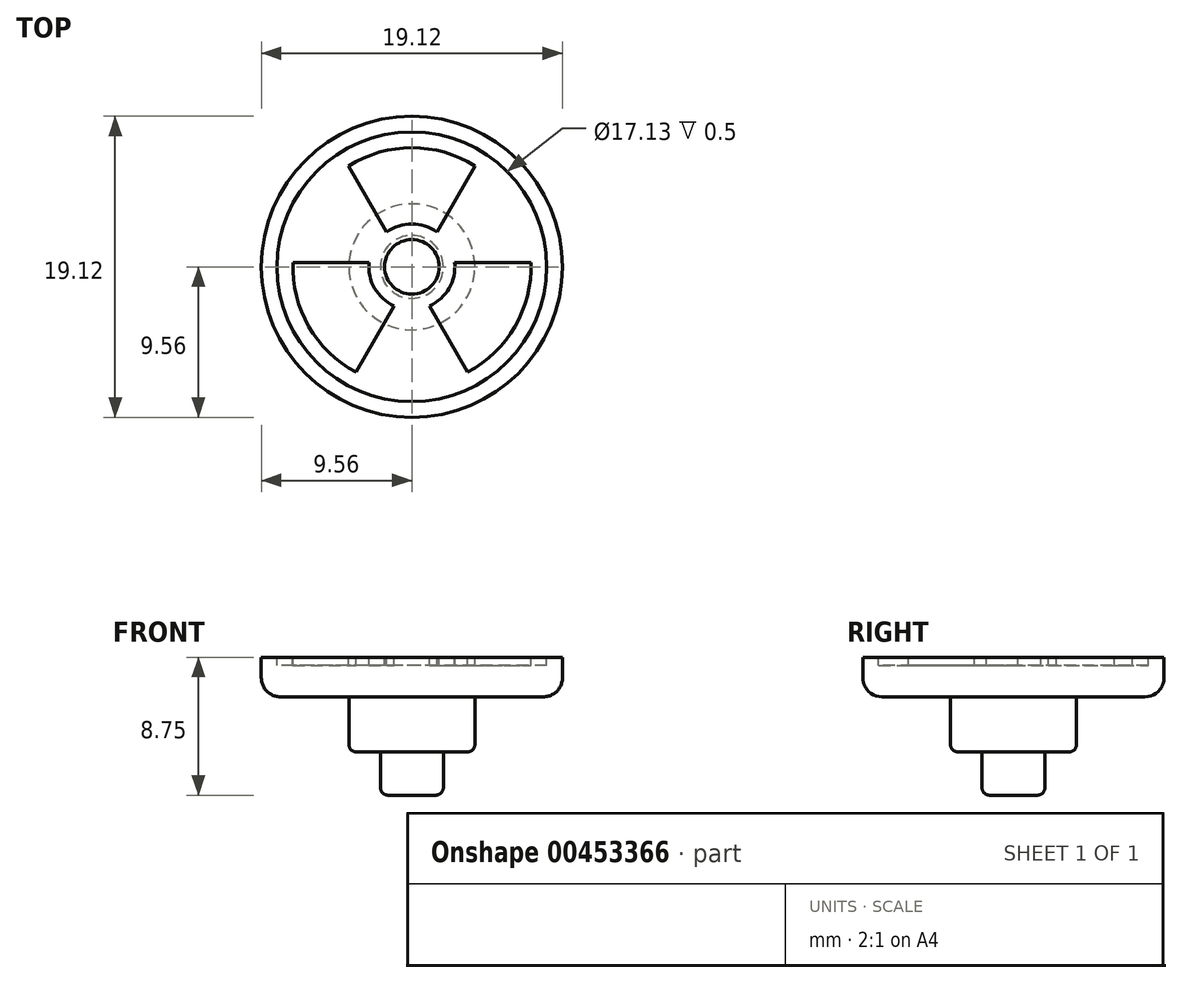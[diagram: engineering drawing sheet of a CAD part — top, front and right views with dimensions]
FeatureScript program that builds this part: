
annotation { "Feature Type Name" : "Feature", "Feature Type Description" : "" }
export const myFeature = defineFeature(function(context is Context, id is Id, definition is map)
    precondition{}
    {
        {
            var Q0;
            Q0=qCreatedBy(makeId("Top.planeOp"),FACE);
            var sketch = newSketch(context, id + "F0", { "sketchPlane" : qUnion([Q0])});
            skCircle(sketch, "E0", {"center": v(0, 0) * mm, "radius": 9.56 * mm});
            skSolve(sketch);
        }
        {
            var Q0;
            Q0=makeQuery(id+"F0.imprint","IMPRINT",FACE,{"disambiguationData":[TD([[makeQuery(id+"F0.imprint","IMPRINT",EDGE,{"derivedFrom":sQuery(id+"F0.wireOp",EDGE,"E0")}),1.0]])]});
            extrude(context, id + "F1", {"entities" : qUnion([Q0]), "depth" : 2.5 * mm, "offsetDistance" : 25 * mm});
        }
        {
            var Q0;
            Q0=makeQuery(id+"F1.opExtrude","CAP_FACE",FACE,{"disambiguationData":[OSD([sQuery(id+"F0.wireOp",EDGE,"E0")])],"isStart":false});
            var sketch = newSketch(context, id + "F2", { "sketchPlane" : qUnion([Q0])});
            skCircle(sketch, "E1", {"center": v(0, 0) * mm, "radius": 1.73 * mm});
            skArc(sketch, "E2", {"start": v(1.6, 2.22) * mm, "mid": v(0, 2.73) * mm, "end": v(-1.6, 2.22) * mm});
            skLineSegment(sketch, "E3", {"start": v(-1.6, 2.22) * mm, "end": v(-4.52, 7.28) * mm});
            skLineSegment(sketch, "E4", {"start": v(1.6, 2.22) * mm, "end": v(4.52, 7.28) * mm});
            skArc(sketch, "E5", {"start": v(4.52, 7.28) * mm, "mid": v(0, 8.56) * mm, "end": v(-4.52, 7.28) * mm});
            skLineSegment(sketch, "E6", {"start": v(0, 0) * mm, "end": v(8.28, 4.78) * mm, "construction": true});
            skLineSegment(sketch, "E7", {"start": v(0, 0) * mm, "end": v(-8.28, 4.78) * mm, "construction": true});
            skLineSegment(sketch, "E8", {"start": v(0, 0) * mm, "end": v(0, -15.04) * mm, "construction": true});
            skLineSegment(sketch, "E9.MirrorCS", {"start": v(2.72, 0.27) * mm, "end": v(8.56, 0.27) * mm});
            skArc(sketch, "E10.MirrorCS", {"start": v(2.72, 0.27) * mm, "mid": v(2.36, -1.36) * mm, "end": v(1.12, -2.49) * mm});
            skLineSegment(sketch, "E11.MirrorCS", {"start": v(1.12, -2.49) * mm, "end": v(4.04, -7.55) * mm});
            skArc(sketch, "E12.MirrorCS", {"start": v(8.56, 0.27) * mm, "mid": v(7.42, -4.28) * mm, "end": v(4.04, -7.55) * mm});
            skLineSegment(sketch, "E13.MirrorCS", {"start": v(-2.72, 0.27) * mm, "end": v(-8.56, 0.27) * mm});
            skArc(sketch, "E14.MirrorCS", {"start": v(-1.12, -2.49) * mm, "mid": v(-2.36, -1.36) * mm, "end": v(-2.72, 0.27) * mm});
            skLineSegment(sketch, "E15.MirrorCS", {"start": v(-1.12, -2.49) * mm, "end": v(-4.04, -7.55) * mm});
            skArc(sketch, "E16.MirrorCS", {"start": v(-4.04, -7.55) * mm, "mid": v(-7.42, -4.28) * mm, "end": v(-8.56, 0.27) * mm});
            skCircle(sketch, "E17", {"center": v(0, 0) * mm, "radius": 8.56 * mm});
            skCircle(sketch, "E18", {"center": v(0, 0) * mm, "radius": 7.56 * mm});
            skSolve(sketch);
        }
        {
            var Q0;
            {var subQ0=sQuery(id+"F2.wireOp",EDGE,"E17");var subQ1=sQuery(id+"F2.wireOp",EDGE,"E3");var subQ2=makeQuery(id+"F2.imprint","INTERSECT",VERTEX,{"derivedFrom":[subQ1,subQ0]});Q0=makeQuery(id+"F2.imprint","IMPRINT",FACE,{"disambiguationData":[TD([[makeQuery(id+"F2.imprint","IMPRINT",EDGE,{"disambiguationData":[TD([[subQ2,1.0]])],"derivedFrom":subQ1}),1.0]])]});}
            var Q1;
            {var subQ0=sQuery(id+"F2.wireOp",EDGE,"E17");var subQ1=sQuery(id+"F2.wireOp",EDGE,"E3");var subQ2=makeQuery(id+"F2.imprint","INTERSECT",VERTEX,{"derivedFrom":[subQ1,subQ0]});Q1=makeQuery(id+"F2.imprint","IMPRINT",FACE,{"disambiguationData":[TD([[makeQuery(id+"F2.imprint","IMPRINT",EDGE,{"disambiguationData":[TD([[subQ2,1.0]])],"derivedFrom":subQ1}),-1.0]])]});}
            var Q2;
            {var subQ0=sQuery(id+"F2.wireOp",EDGE,"E17");var subQ1=sQuery(id+"F2.wireOp",EDGE,"E4");var subQ2=makeQuery(id+"F2.imprint","INTERSECT",VERTEX,{"derivedFrom":[subQ1,subQ0]});Q2=makeQuery(id+"F2.imprint","IMPRINT",FACE,{"disambiguationData":[TD([[makeQuery(id+"F2.imprint","IMPRINT",EDGE,{"disambiguationData":[TD([[subQ2,1.0]])],"derivedFrom":subQ1}),-1.0]])]});}
            var Q3;
            {var subQ0=sQuery(id+"F2.wireOp",EDGE,"E17");var subQ1=sQuery(id+"F2.wireOp",EDGE,"E9.MirrorCS");var subQ2=makeQuery(id+"F2.imprint","INTERSECT",VERTEX,{"derivedFrom":[subQ1,subQ0]});Q3=makeQuery(id+"F2.imprint","IMPRINT",FACE,{"disambiguationData":[TD([[makeQuery(id+"F2.imprint","IMPRINT",EDGE,{"disambiguationData":[TD([[subQ2,1.0]])],"derivedFrom":subQ1}),-1.0]])]});}
            var Q4;
            {var subQ0=sQuery(id+"F2.wireOp",EDGE,"E17");var subQ1=sQuery(id+"F2.wireOp",EDGE,"E11.MirrorCS");var subQ2=makeQuery(id+"F2.imprint","INTERSECT",VERTEX,{"derivedFrom":[subQ1,subQ0]});Q4=makeQuery(id+"F2.imprint","IMPRINT",FACE,{"disambiguationData":[TD([[makeQuery(id+"F2.imprint","IMPRINT",EDGE,{"disambiguationData":[TD([[subQ2,1.0]])],"derivedFrom":subQ1}),-1.0]])]});}
            var Q5;
            {var subQ0=sQuery(id+"F2.wireOp",EDGE,"E17");var subQ1=sQuery(id+"F2.wireOp",EDGE,"E13.MirrorCS");var subQ2=makeQuery(id+"F2.imprint","INTERSECT",VERTEX,{"derivedFrom":[subQ1,subQ0]});Q5=makeQuery(id+"F2.imprint","IMPRINT",FACE,{"disambiguationData":[TD([[makeQuery(id+"F2.imprint","IMPRINT",EDGE,{"disambiguationData":[TD([[subQ2,1.0]])],"derivedFrom":subQ1}),1.0]])]});}
            var Q6;
            Q6=makeQuery(id+"F2.imprint","IMPRINT",FACE,{"disambiguationData":[TD([[makeQuery(id+"F2.imprint","IMPRINT",EDGE,{"derivedFrom":sQuery(id+"F2.wireOp",EDGE,"E1")}),-1.0]])]});
            extrude(context, id + "F3", {"entities" : qUnion([Q0, Q1, Q2, Q3, Q4, Q5, Q6]), "operationType" : NewBodyOperationType.REMOVE, "oppositeDirection" : true, "depth" : .5 * mm, "offsetDistance" : 25 * mm});
        }
        {
            var Q0;
            Q0=makeQuery(id+"F1.opExtrude","CAP_FACE",FACE,{"disambiguationData":[OSD([sQuery(id+"F0.wireOp",EDGE,"E0")])],"isStart":true});
            var sketch = newSketch(context, id + "F4", { "sketchPlane" : qUnion([Q0])});
            skCircle(sketch, "E19", {"center": v(0, 0) * mm, "radius": 4 * mm});
            skSolve(sketch);
        }
        {
            var Q0;
            Q0=makeQuery(id+"F4.imprint","IMPRINT",FACE,{"disambiguationData":[TD([[makeQuery(id+"F4.imprint","IMPRINT",EDGE,{"derivedFrom":sQuery(id+"F4.wireOp",EDGE,"E19")}),1.0]])]});
            extrude(context, id + "F5", {"entities" : qUnion([Q0]), "operationType" : NewBodyOperationType.ADD, "depth" : 3.5 * mm, "offsetDistance" : 25 * mm});
        }
        {
            var Q0;
            Q0=makeQuery(id+"F1.opExtrude","CAP_EDGE",EDGE,{"disambiguationData":[OSD([sQuery(id+"F0.wireOp",EDGE,"E0")])],"isStart":true});
            fillet(context, id + "F6", {"entities" : qUnion([Q0]), "radius" : 1.2 * mm, "tangentPropagation" : true, "allowEdgeOverflow" : false});
        }
        {
            var Q0;
            Q0=makeQuery(id+"F5.opExtrude","CAP_FACE",FACE,{"disambiguationData":[OSD([sQuery(id+"F4.wireOp",EDGE,"E19")])],"isStart":false});
            var sketch = newSketch(context, id + "F7", { "sketchPlane" : qUnion([Q0])});
            skCircle(sketch, "E20", {"center": v(0, 0) * mm, "radius": 2 * mm});
            skSolve(sketch);
        }
        {
            var Q0;
            Q0=makeQuery(id+"F7.imprint","IMPRINT",FACE,{"disambiguationData":[TD([[makeQuery(id+"F7.imprint","IMPRINT",EDGE,{"derivedFrom":sQuery(id+"F7.wireOp",EDGE,"E20")}),1.0]])]});
            extrude(context, id + "F8", {"entities" : qUnion([Q0]), "operationType" : NewBodyOperationType.ADD, "depth" : 2.75 * mm, "offsetDistance" : 25 * mm});
        }
        {
            var Q0;
            Q0=makeQuery(id+"F8.opExtrude","CAP_EDGE",EDGE,{"disambiguationData":[OSD([sQuery(id+"F7.wireOp",EDGE,"E20")])],"isStart":false});
            fillet(context, id + "F9", {"entities" : qUnion([Q0]), "radius" : 0.48 * mm, "tangentPropagation" : true, "allowEdgeOverflow" : false});
        }
        {
            var Q0;
            Q0=makeQuery(id+"F5.opExtrude","CAP_EDGE",EDGE,{"disambiguationData":[OSD([sQuery(id+"F4.wireOp",EDGE,"E19")])],"isStart":false});
            fillet(context, id + "F10", {"entities" : qUnion([Q0]), "radius" : 0.46 * mm, "tangentPropagation" : true, "allowEdgeOverflow" : false});
        }
    });
